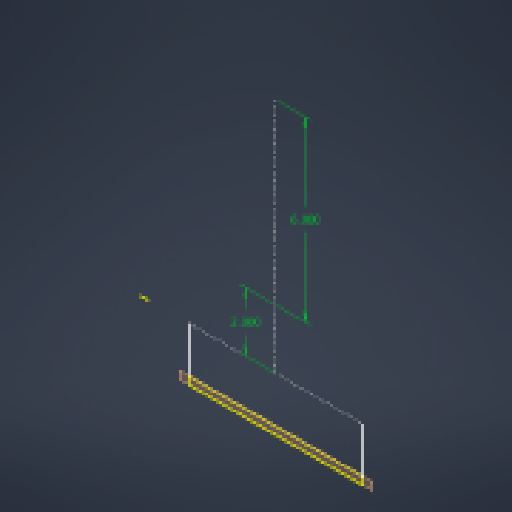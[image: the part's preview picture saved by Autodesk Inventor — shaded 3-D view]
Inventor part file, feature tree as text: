
AUTODESK INVENTOR PART (.ipt)
format: ipt  version: 2024 (Build 280153000, 153)  size: 115,712 bytes
history: native  units: in
note: dims shown in document units (in); Inventor stores cm internally (conversion verified against a paired STEP export)
features: other x6, reference x2, plane x1, sketch x1
ambient origin geometry x8: Origin, YZ Plane, XZ Plane, XY Plane, X Axis, Y Axis, Z Axis, Center Point
feature tree (10):
  plane  "Work Plane1"
  sketch  "Sketch1"  dims[d0=2.0in d1=6.0in]
  reference  "Reference1"
  reference  "Reference2"
  other  "<userpath>\CodingProjects\C-AAM\CAD\V1\Parts\2ndAxis.iam"
  other  "2ndAxis.iam"
  other  "AxisBoard:1"
  other  "<userpath>\CodingProjects\C-AAM\CAD\V1\Base.iam"
  other  "Base.iam"
  other  "6627T91_Stepper Motor:1"
